# Revit family: Lin
name_source: partatom
category: Lighting Fixtures
units: mm (PartAtom-declared; Revit-internal decimal feet)

## family parameters
Cut with Voids When Loaded = Yes
Host = Face
Light Source = Yes
Maintain Annotation Orientation = No
Part Type = Normal
Room Calculation Point = No
Round Connector Dimension = Use Diameter
Shared = No

## types (5) — shared parameters
Beam Angle = 0.00°
CRI = 90
Color Filter = 16777215
Default Elevation = 0' - 3 5/16"
Dimming Lamp Color Temperature Shift = <None>
Lamp = LED
Load Classification = Lighting
Manufacturer = Above All Lighting
Power Factor = 0.9
Tilt Angle = 90.00°
URL = https://www.abovealllighting.com

## per-type parameters (varying)
| type | Length | Model | Photometric Web File | Wattage Comments |
| LIN-4W-3000K-90CRI | 0' - 3 5/16" | LIN04-3090-24V-DL-MTM-BK | LIN04-3090-DL.IES | 4W |
| LIN-7W-3000K-90CRI | 0' - 6 15/32" | LIN07-3090-24V-DL-MTM-BK | LIN07-3090-DL.IES | 7W |
| LIN-13W-3000K-90CRI | 1' - 0 3/4" | LIN13-3090-24V-DL-MTM-BK | LIN13-3090-DL.IES | 13W |
| LIN-26W-3000K-90CRI | 2' - 1 3/16" | LIN26-3090-24V-DL-MTM-BK | LIN26-3090-DL.IES | 26W |
| LIN-39W-3000K-90CRI | 3' - 1 13/16" | LIN26-3090-24V-DL-MTM-BK | LIN39-3090-DL.IES | 39W |

## geometry (parser evidence)
native form markers: Sweep x3
no freeform markers — native parametric forms only
